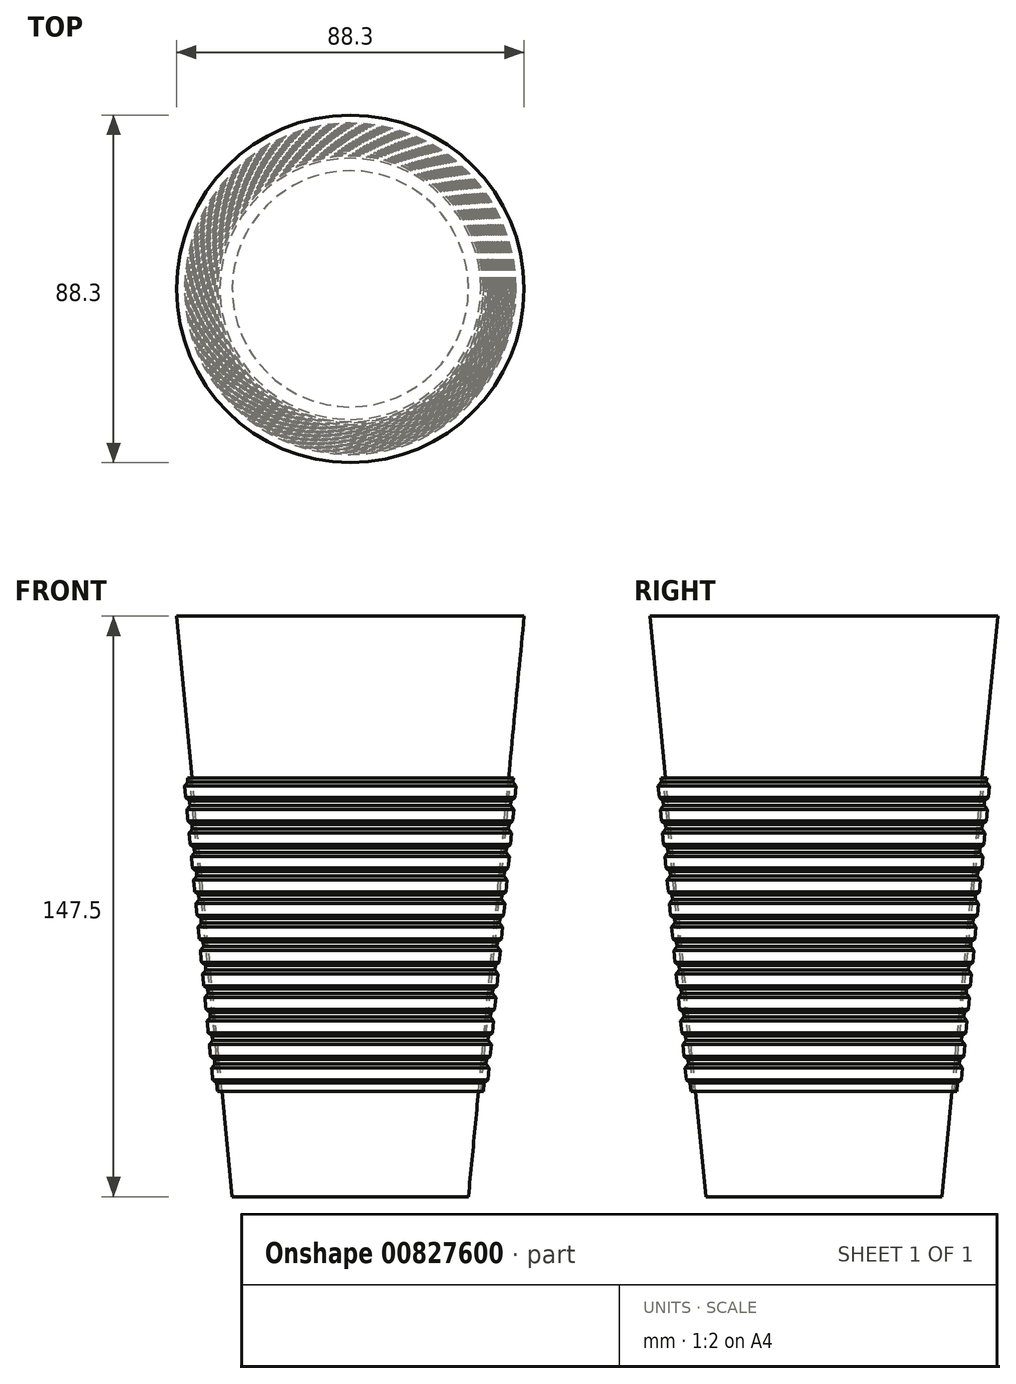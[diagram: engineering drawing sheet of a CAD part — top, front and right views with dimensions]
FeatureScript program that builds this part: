
annotation { "Feature Type Name" : "Feature", "Feature Type Description" : "" }
export const myFeature = defineFeature(function(context is Context, id is Id, definition is map)
    precondition{}
    {
        {
            var Q0;
            Q0=qCreatedBy(makeId("Top.planeOp"),FACE);
            var sketch = newSketch(context, id + "F0", { "sketchPlane" : qUnion([Q0])});
            skCircle(sketch, "E0", {"center": v(0, 0) * mm, "radius": 30 * mm});
            skSolve(sketch);
        }
        {
            var Q0;
            Q0=qCreatedBy(makeId("Top.planeOp"),FACE);
            cPlane(context, id + "F1", {"entities" : qUnion([Q0]), "cplaneType" : CPlaneType.OFFSET, "offset" : 147.5 * mm, "width" : 150 * mm, "height" : 150 * mm});
        }
        {
            var Q0;
            Q0=qCreatedBy(id+"F1.planeOp",FACE);
            var sketch = newSketch(context, id + "F2", { "sketchPlane" : qUnion([Q0])});
            skCircle(sketch, "E1", {"center": v(0, 0) * mm, "radius": 44.15 * mm});
            skSolve(sketch);
        }
        {
            var Q0;
            Q0=makeQuery(id+"F0.imprint","IMPRINT",FACE,{"disambiguationData":[TD([[makeQuery(id+"F0.imprint","IMPRINT",EDGE,{"derivedFrom":sQuery(id+"F0.wireOp",EDGE,"E0")}),1.0]])]});
            var Q1;
            Q1=makeQuery(id+"F2.imprint","IMPRINT",FACE,{"disambiguationData":[TD([[makeQuery(id+"F2.imprint","IMPRINT",EDGE,{"derivedFrom":sQuery(id+"F2.wireOp",EDGE,"E1")}),1.0]])]});
            loft(context, id + "F3", {"sheetProfilesArray" : [{ "sheetProfileEntities" : qUnion([Q0]) }, { "sheetProfileEntities" : qUnion([Q1]) }]});
        }
        {
            var Q0;
            Q0=qCreatedBy(makeId("Front.planeOp"),FACE);
            var sketch = newSketch(context, id + "F4", { "sketchPlane" : qUnion([Q0])});
            skLineSegment(sketch, "E2", {"start": v(44.15, 147.5) * mm, "end": v(30, 0) * mm, "construction": true});
            skLineSegment(sketch, "E3", {"start": v(-30, 0) * mm, "end": v(-44.15, 147.5) * mm, "construction": true});
            skLineSegment(sketch, "E4", {"start": v(0, 0) * mm, "end": v(0, 147.5) * mm, "construction": true});
            skLineSegment(sketch, "E5", {"start": v(-40.21, 106.44) * mm, "end": v(-40.81, 106.44) * mm, "construction": true});
            skLineSegment(sketch, "E6", {"start": v(-40.81, 106.44) * mm, "end": v(-33.18, 26.86) * mm});
            skLineSegment(sketch, "E7", {"start": v(-33.18, 26.86) * mm, "end": v(-33.77, 26.8) * mm});
            skLineSegment(sketch, "E8", {"start": v(-33.77, 26.8) * mm, "end": v(-41.41, 106.44) * mm});
            skLineSegment(sketch, "E9", {"start": v(-41.41, 106.44) * mm, "end": v(-40.81, 106.44) * mm});
            skLineSegment(sketch, "E10", {"start": v(-41.41, 106.44) * mm, "end": v(-41.22, 104.44) * mm, "construction": true});
            skLineSegment(sketch, "E11", {"start": v(-41.22, 104.44) * mm, "end": v(-42.12, 104.36) * mm, "construction": true});
            skLineSegment(sketch, "E12", {"start": v(-42.12, 104.36) * mm, "end": v(-41.83, 101.37) * mm});
            skLineSegment(sketch, "E13", {"start": v(-41.83, 101.37) * mm, "end": v(-40.85, 100.56) * mm});
            skLineSegment(sketch, "E14", {"start": v(-42.12, 104.36) * mm, "end": v(-41.3, 105.34) * mm});
            skLineSegment(sketch, "E15.1.0.0", {"start": v(-41.54, 98.39) * mm, "end": v(-40.73, 99.37) * mm});
            skLineSegment(sketch, "E15.1.0.1", {"start": v(-41.54, 98.39) * mm, "end": v(-41.26, 95.4) * mm});
            skLineSegment(sketch, "E15.1.0.2", {"start": v(-41.26, 95.4) * mm, "end": v(-40.27, 94.6) * mm});
            skLineSegment(sketch, "E15.2.0.0", {"start": v(-40.97, 92.41) * mm, "end": v(-40.16, 93.4) * mm});
            skLineSegment(sketch, "E15.2.0.1", {"start": v(-40.97, 92.41) * mm, "end": v(-40.68, 89.43) * mm});
            skLineSegment(sketch, "E15.2.0.2", {"start": v(-40.68, 89.43) * mm, "end": v(-39.7, 88.62) * mm});
            skLineSegment(sketch, "E15.3.0.0", {"start": v(-40.4, 86.44) * mm, "end": v(-39.59, 87.42) * mm});
            skLineSegment(sketch, "E15.3.0.1", {"start": v(-40.4, 86.44) * mm, "end": v(-40.11, 83.45) * mm});
            skLineSegment(sketch, "E15.3.0.2", {"start": v(-40.11, 83.45) * mm, "end": v(-39.13, 82.65) * mm});
            skLineSegment(sketch, "E15.direction1", {"start": v(-42.12, 104.36) * mm, "end": v(-41.54, 98.39) * mm, "construction": true});
            skLineSegment(sketch, "E16.0.4.0", {"start": v(-39.82, 80.47) * mm, "end": v(-39.01, 81.45) * mm});
            skLineSegment(sketch, "E16.3.4.0", {"start": v(-39.82, 80.47) * mm, "end": v(-39.54, 77.48) * mm});
            skLineSegment(sketch, "E16.6.4.0", {"start": v(-39.54, 77.48) * mm, "end": v(-38.56, 76.67) * mm});
            skLineSegment(sketch, "E16.0.5.0", {"start": v(-39.25, 74.5) * mm, "end": v(-38.44, 75.48) * mm});
            skLineSegment(sketch, "E16.3.5.0", {"start": v(-39.25, 74.5) * mm, "end": v(-38.96, 71.5) * mm});
            skLineSegment(sketch, "E16.6.5.0", {"start": v(-38.96, 71.5) * mm, "end": v(-37.98, 70.7) * mm});
            skLineSegment(sketch, "E16.0.6.0", {"start": v(-38.68, 68.52) * mm, "end": v(-37.87, 69.5) * mm});
            skLineSegment(sketch, "E16.3.6.0", {"start": v(-38.68, 68.52) * mm, "end": v(-38.4, 65.54) * mm});
            skLineSegment(sketch, "E16.6.6.0", {"start": v(-38.4, 65.54) * mm, "end": v(-37.4, 64.73) * mm});
            skLineSegment(sketch, "E16.0.7.0", {"start": v(-38.1, 62.55) * mm, "end": v(-37.3, 63.53) * mm});
            skLineSegment(sketch, "E16.3.7.0", {"start": v(-38.1, 62.55) * mm, "end": v(-37.82, 59.56) * mm});
            skLineSegment(sketch, "E16.6.7.0", {"start": v(-37.82, 59.56) * mm, "end": v(-36.84, 58.75) * mm});
            skLineSegment(sketch, "E16.0.8.0", {"start": v(-37.53, 56.58) * mm, "end": v(-36.72, 57.56) * mm});
            skLineSegment(sketch, "E16.3.8.0", {"start": v(-37.53, 56.58) * mm, "end": v(-37.25, 53.6) * mm});
            skLineSegment(sketch, "E16.6.8.0", {"start": v(-37.25, 53.6) * mm, "end": v(-36.26, 52.78) * mm});
            skLineSegment(sketch, "E16.0.9.0", {"start": v(-36.96, 50.6) * mm, "end": v(-36.15, 51.59) * mm});
            skLineSegment(sketch, "E16.3.9.0", {"start": v(-36.96, 50.6) * mm, "end": v(-36.67, 47.62) * mm});
            skLineSegment(sketch, "E16.6.9.0", {"start": v(-36.67, 47.62) * mm, "end": v(-35.7, 46.8) * mm});
            skLineSegment(sketch, "E16.0.10.0", {"start": v(-36.39, 44.63) * mm, "end": v(-35.58, 45.62) * mm});
            skLineSegment(sketch, "E16.3.10.0", {"start": v(-36.39, 44.63) * mm, "end": v(-36.1, 41.65) * mm});
            skLineSegment(sketch, "E16.6.10.0", {"start": v(-36.1, 41.65) * mm, "end": v(-35.12, 40.84) * mm});
            skLineSegment(sketch, "E16.0.11.0", {"start": v(-35.81, 38.66) * mm, "end": v(-35, 39.64) * mm});
            skLineSegment(sketch, "E16.3.11.0", {"start": v(-35.81, 38.66) * mm, "end": v(-35.53, 35.67) * mm});
            skLineSegment(sketch, "E16.6.11.0", {"start": v(-35.53, 35.67) * mm, "end": v(-34.54, 34.86) * mm});
            skLineSegment(sketch, "E17.0.12.0", {"start": v(-35.24, 32.69) * mm, "end": v(-34.43, 33.67) * mm});
            skLineSegment(sketch, "E17.3.12.0", {"start": v(-35.24, 32.69) * mm, "end": v(-34.95, 29.7) * mm});
            skLineSegment(sketch, "E17.6.12.0", {"start": v(-34.95, 29.7) * mm, "end": v(-33.97, 28.9) * mm});
            skSolve(sketch);
        }
        {
            var Q0;
            Q0 = qSketchRegion(id + "F4", true);
            var Q1;
            Q1=sQuery(id+"F4.wireOp",EDGE,"E4");
            revolve(context, id + "F5", {"entities" : qUnion([Q0]), "axis" : qUnion([Q1]), "revolveType" : RevolveType.FULL, "surfaceOperationType" : NewSurfaceOperationType.NEW});
        }
    });
